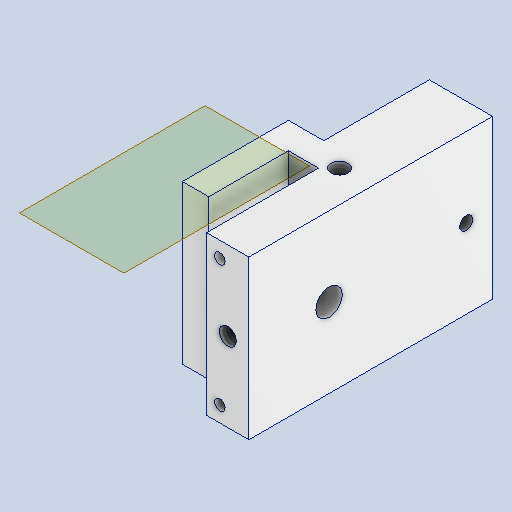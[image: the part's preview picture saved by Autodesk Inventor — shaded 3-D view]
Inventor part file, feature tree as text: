
AUTODESK INVENTOR PART (.ipt)
format: ipt  version: 2025 (Build 290162010, 162A)  size: 257,024 bytes
history: native  units: mm
features: sketch x10, reference x10, hole x9, other x6, projected_geometry x3, plane x1, extrude x1
ambient origin geometry x8: Origin, YZ Plane, XZ Plane, XY Plane, X Axis, Y Axis, Z Axis, Center Point
bodies: Volumenkörper1 (feature_tree)
feature tree (40):
  plane  "Arbeitsebene1"
  extrude  "Extrusion1"  Depth=5.0mm
  hole  "gewindeLastPunkt"  [1 undecoded]
  hole  "Katzeverbindung"  [1 undecoded]
  hole  "Zentrierbolzen"  [1 undecoded]
  hole  "seilV"  [1 undecoded]
  hole  "GLVV"  [1 undecoded]
  hole  "GLVO"  [1 undecoded]
  hole  "GLVU"  [1 undecoded]
  hole  "DLVU"  [1 undecoded]
  hole  "DLVO"  [1 undecoded]
  sketch  "Skizze1"  dims[d0=20.0mm d1=5.0mm]
  reference  "Referenz1"
  reference  "Referenz2"
  reference  "Referenz3"
  reference  "Referenz4"
  sketch  "Skizze2"  dims[d2=5.0mm d3=13.0mm]
  sketch  "Skizze3"  dims[d4=30.0mm d5=0.0mm d6=5.0mm]
  reference  "Referenz5"
  sketch  "Skizze4"  dims[d18=12.0mm]
  reference  "Referenz6"
  reference  "Referenz7"
  sketch  "Skizze5"  dims[d19=2.459mm d20=6.0mm d21=4.0mm d22=2.0mm d23=90.0deg d24=8.0mm d25=20.594885mm]
  sketch  "Skizze6"  dims[d28=3.242mm d29=8.0mm d30=7.4mm d31=15.0mm d32=90.0deg d33=11.8mm d34=20.594885mm]
  projected_geometry  "Projizierte Kontur2"
  sketch  "Skizze7"  dims[d35=2.0mm d36=6.0mm d37=4.0mm d38=2.0mm d39=90.0deg d40=6.0mm d41=20.594885mm]
  reference  "Referenz8"
  projected_geometry  "Projizierte Kontur3"
  sketch  "Skizze8"  dims[d45=3.242mm d46=9.0mm d47=4.0mm d48=2.0mm d49=90.0deg d50=8.0mm d51=20.594885mm]
  projected_geometry  "Projizierte Kontur4"
  reference  "Referenz9"
  sketch  "Skizze9"  dims[d54=1.567mm d55=2.5mm d56=4.0mm d57=2.0mm d58=90.0deg d59=4.0mm d60=20.594885mm d62=9.0mm]
  reference  "Referenz10"
  sketch  "Skizze10"  dims[d63=1.567mm d64=2.5mm d65=4.0mm d66=2.0mm d67=90.0deg d68=4.0mm d69=20.594885mm d70=4.0mm d71=1.567mm d72=2.5mm d73=4.0mm d74=2.0mm d75=90.0deg d76=4.0mm d77=20.594885mm d78=5.0mm d79=6.0mm d80=4.0mm d81=2.0mm d82=90.0deg d83=8.0mm d84=0.0mm d85=5.0mm d86=6.0mm d87=4.0mm d88=2.0mm d89=90.0deg d90=8.0mm d91=0.0mm d92=6.0mm d93=23.0mm]
  other  "<userpath>\Documents\Inventor\Krandemonstrator\Demonstrator.iam"
  other  "Demonstrator.iam"
  other  "Träger:1"
  other  "Katze_Lagerhalter_hinten:1"
  other  "LagerVV:1"
  other  "LagerVO:1"
note: 9 required parameter values undecoded (feature->parameter linkage not recoverable at this tier; creation-order binding heuristic only, values carry confidence <= 0.55)
